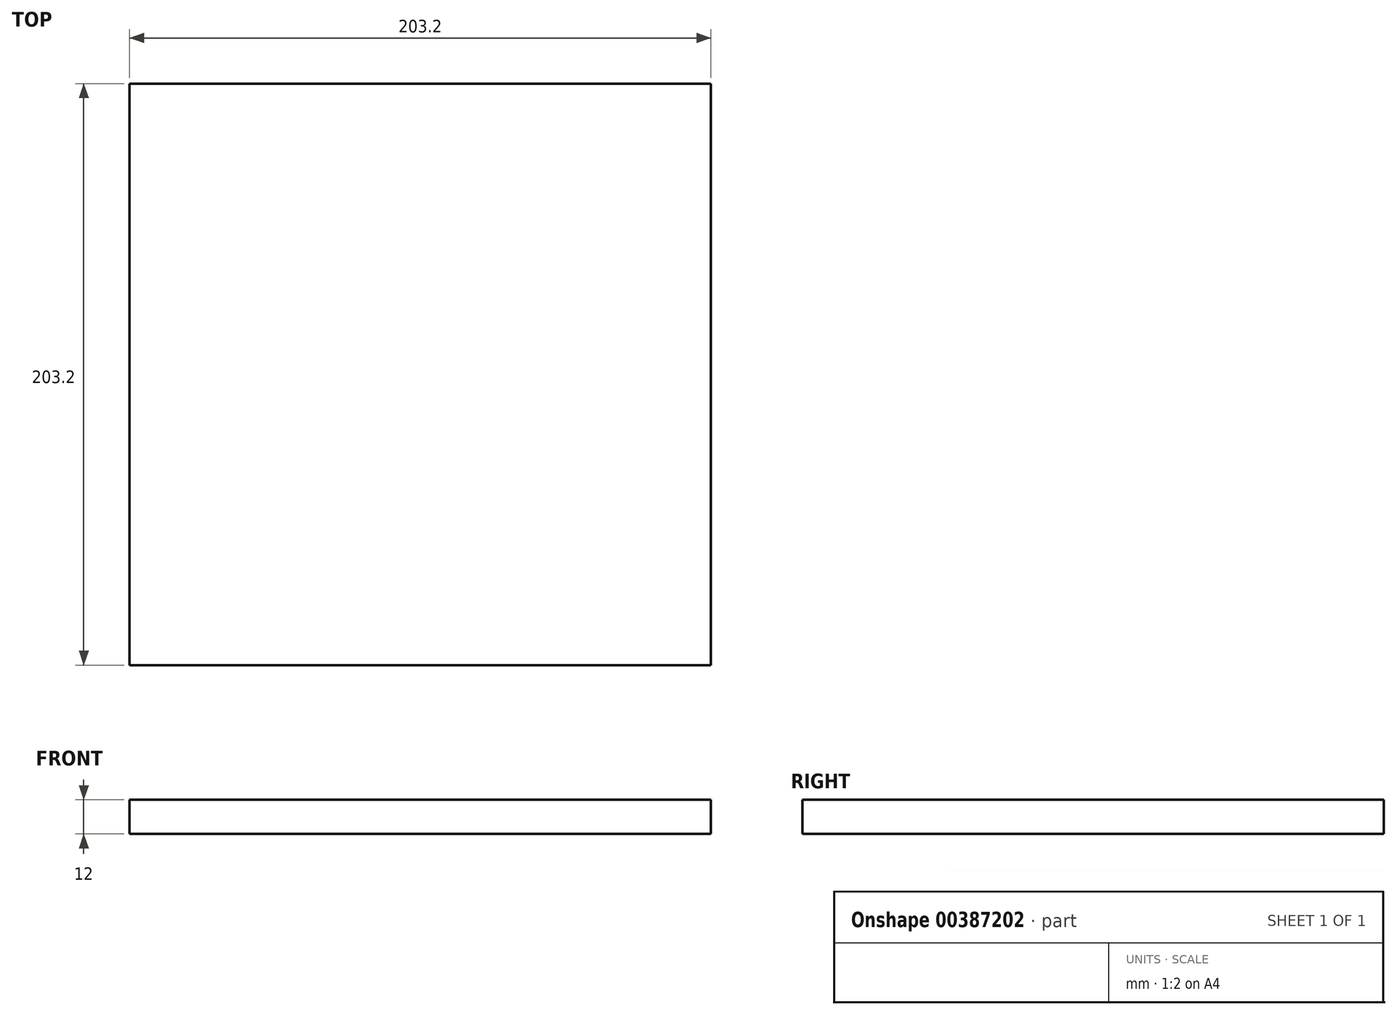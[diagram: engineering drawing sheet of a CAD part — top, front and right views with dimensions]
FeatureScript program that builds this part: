
annotation { "Feature Type Name" : "Feature", "Feature Type Description" : "" }
export const myFeature = defineFeature(function(context is Context, id is Id, definition is map)
    precondition{}
    {
        {
            var Q0;
            Q0=qCreatedBy(makeId("Top.planeOp"),FACE);
            var sketch = newSketch(context, id + "F0", { "sketchPlane" : qUnion([Q0])});
            skLineSegment(sketch, "E0.bottom", {"start": v(-109.86, 147.9) * mm, "end": v(93.34, 147.9) * mm});
            skLineSegment(sketch, "E0.top", {"start": v(-109.86, -55.3) * mm, "end": v(93.34, -55.3) * mm});
            skLineSegment(sketch, "E0.left", {"start": v(-109.86, 147.9) * mm, "end": v(-109.86, -55.3) * mm});
            skLineSegment(sketch, "E0.right", {"start": v(93.34, 147.9) * mm, "end": v(93.34, -55.3) * mm});
            skLineSegment(sketch, "E1.bottom", {"start": v(93.34, -55.3) * mm, "end": v(-109.86, -55.3) * mm});
            skSolve(sketch);
        }
        {
            var Q0;
            Q0=makeQuery(id+"F0.imprint","IMPRINT",FACE,{"disambiguationData":[TD([[makeQuery(id+"F0.imprint","IMPRINT",EDGE,{"derivedFrom":sQuery(id+"F0.wireOp",EDGE,"E0.bottom")}),-1.0]])]});
            extrude(context, id + "F1", {"entities" : qUnion([Q0]), "depth" : 12 * mm});
        }
    });
